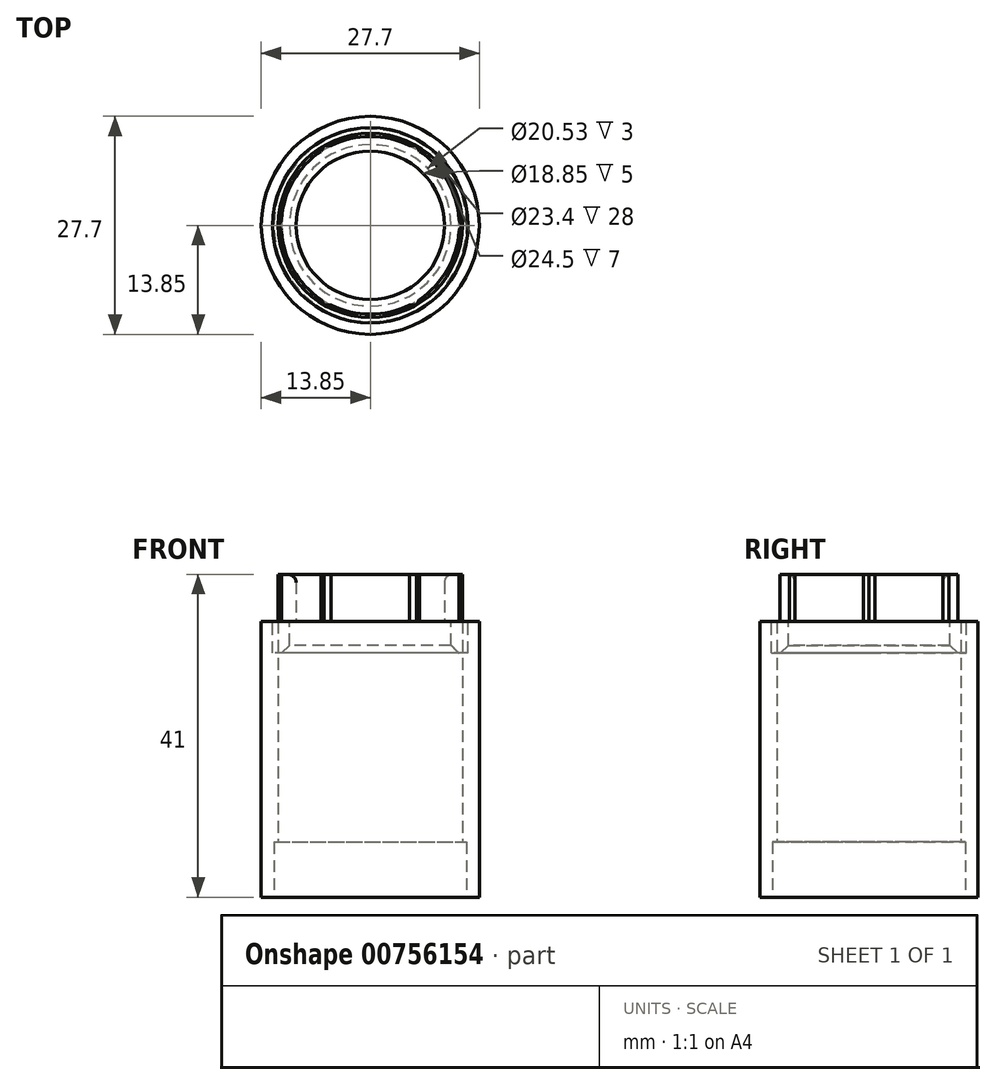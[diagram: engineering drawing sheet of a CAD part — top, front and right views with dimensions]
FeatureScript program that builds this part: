
annotation { "Feature Type Name" : "Feature", "Feature Type Description" : "" }
export const myFeature = defineFeature(function(context is Context, id is Id, definition is map)
    precondition{}
    {
        {
            var Q0;
            Q0=qCreatedBy(makeId("Top.planeOp"),FACE);
            var sketch = newSketch(context, id + "F0", { "sketchPlane" : qUnion([Q0])});
            skCircle(sketch, "E0", {"center": v(0, 0) * mm, "radius": 13.85 * mm});
            skCircle(sketch, "E1", {"center": v(0, 0) * mm, "radius": 11.7 * mm});
            skSolve(sketch);
        }
        {
            var Q0;
            Q0=makeQuery(id+"F0.imprint","IMPRINT",FACE,{"disambiguationData":[TD([[makeQuery(id+"F0.imprint","IMPRINT",EDGE,{"derivedFrom":sQuery(id+"F0.wireOp",EDGE,"E0")}),1.0]])]});
            extrude(context, id + "F1", {"entities" : qUnion([Q0]), "depth" : 35 * mm, "offsetDistance" : 25 * mm});
        }
        {
            var Q0;
            Q0=makeQuery(id+"F1.opExtrude","CAP_FACE",FACE,{"disambiguationData":[OSD([sQuery(id+"F0.wireOp",EDGE,"E0"),sQuery(id+"F0.wireOp",EDGE,"E1")])],"isStart":false});
            var sketch = newSketch(context, id + "F2", { "sketchPlane" : qUnion([Q0])});
            skCircle(sketch, "E2", {"center": v(0, 0) * mm, "radius": 11.3 * mm});
            skCircle(sketch, "E3.cCircle", {"center": v(0, 0) * mm, "radius": 11.7 * mm, "construction": true});
            skLineSegment(sketch, "E3.0", {"start": v(11.7, 0) * mm, "end": v(5.85, -10.13) * mm});
            skLineSegment(sketch, "E3.1", {"start": v(5.85, -10.13) * mm, "end": v(-5.85, -10.13) * mm});
            skLineSegment(sketch, "E3.2", {"start": v(-5.85, -10.13) * mm, "end": v(-11.7, 0) * mm});
            skLineSegment(sketch, "E3.3", {"start": v(-11.7, 0) * mm, "end": v(-5.85, 10.13) * mm});
            skLineSegment(sketch, "E3.4", {"start": v(-5.85, 10.13) * mm, "end": v(5.85, 10.13) * mm});
            skLineSegment(sketch, "E3.5", {"start": v(5.85, 10.13) * mm, "end": v(11.7, 0) * mm});
            skCircle(sketch, "E4", {"center": v(0, 0) * mm, "radius": 9.43 * mm});
            skSolve(sketch);
        }
        {
            var Q0;
            Q0 = qSketchRegion(id + "F2", true);
            extrude(context, id + "F3", {"entities" : qUnion([Q0]), "depth" : 6 * mm, "offsetDistance" : 25 * mm});
        }
        {
            var Q0;
            Q0=makeQuery(id+"F1.opExtrude","CAP_FACE",FACE,{"disambiguationData":[OSD([sQuery(id+"F0.wireOp",EDGE,"E0"),sQuery(id+"F0.wireOp",EDGE,"E1")])],"isStart":false});
            var sketch = newSketch(context, id + "F4", { "sketchPlane" : qUnion([Q0])});
            skCircle(sketch, "E5", {"center": v(0, 0) * mm, "radius": 12.4 * mm});
            skCircle(sketch, "E6", {"center": v(0, 0) * mm, "radius": 10.27 * mm});
            skSolve(sketch);
        }
        {
            var Q0;
            Q0 = qSketchRegion(id + "F4", true);
            extrude(context, id + "F5", {"entities" : qUnion([Q0]), "oppositeDirection" : true, "depth" : 4 * mm, "offsetDistance" : 25 * mm});
        }
        {
            var Q0;
            Q0=makeQuery(id+"F5.opExtrude","CAP_EDGE",EDGE,{"disambiguationData":[OSD([sQuery(id+"F4.wireOp",EDGE,"E6")])],"isStart":false});
            chamfer(context, id + "F6", {"entities" : qUnion([Q0]), "width" : 1 * mm, "tangentPropagation" : true});
        }
        {
            var Q0;
            Q0=makeQuery(id+"F3.opExtrude","CAP_EDGE",EDGE,{"disambiguationData":[OSD([sQuery(id+"F2.wireOp",EDGE,"E4")])],"isStart":false});
            fillet(context, id + "F7", {"entities" : qUnion([Q0]), "radius" : 1 * mm, "tangentPropagation" : true, "allowEdgeOverflow" : false});
        }
        {
            var Q0;
            Q0=makeQuery(id+"F1.opExtrude","CAP_FACE",FACE,{"disambiguationData":[OSD([sQuery(id+"F0.wireOp",EDGE,"E0"),sQuery(id+"F0.wireOp",EDGE,"E1")])],"isStart":true});
            var sketch = newSketch(context, id + "F8", { "sketchPlane" : qUnion([Q0])});
            skCircle(sketch, "E7", {"center": v(0, 0) * mm, "radius": 12.25 * mm});
            skSolve(sketch);
        }
        {
            var Q0;
            Q0 = qSketchRegion(id + "F8", true);
            extrude(context, id + "F9", {"entities" : qUnion([Q0]), "operationType" : NewBodyOperationType.REMOVE, "oppositeDirection" : true, "depth" : 7 * mm, "offsetDistance" : 25 * mm});
        }
    });
